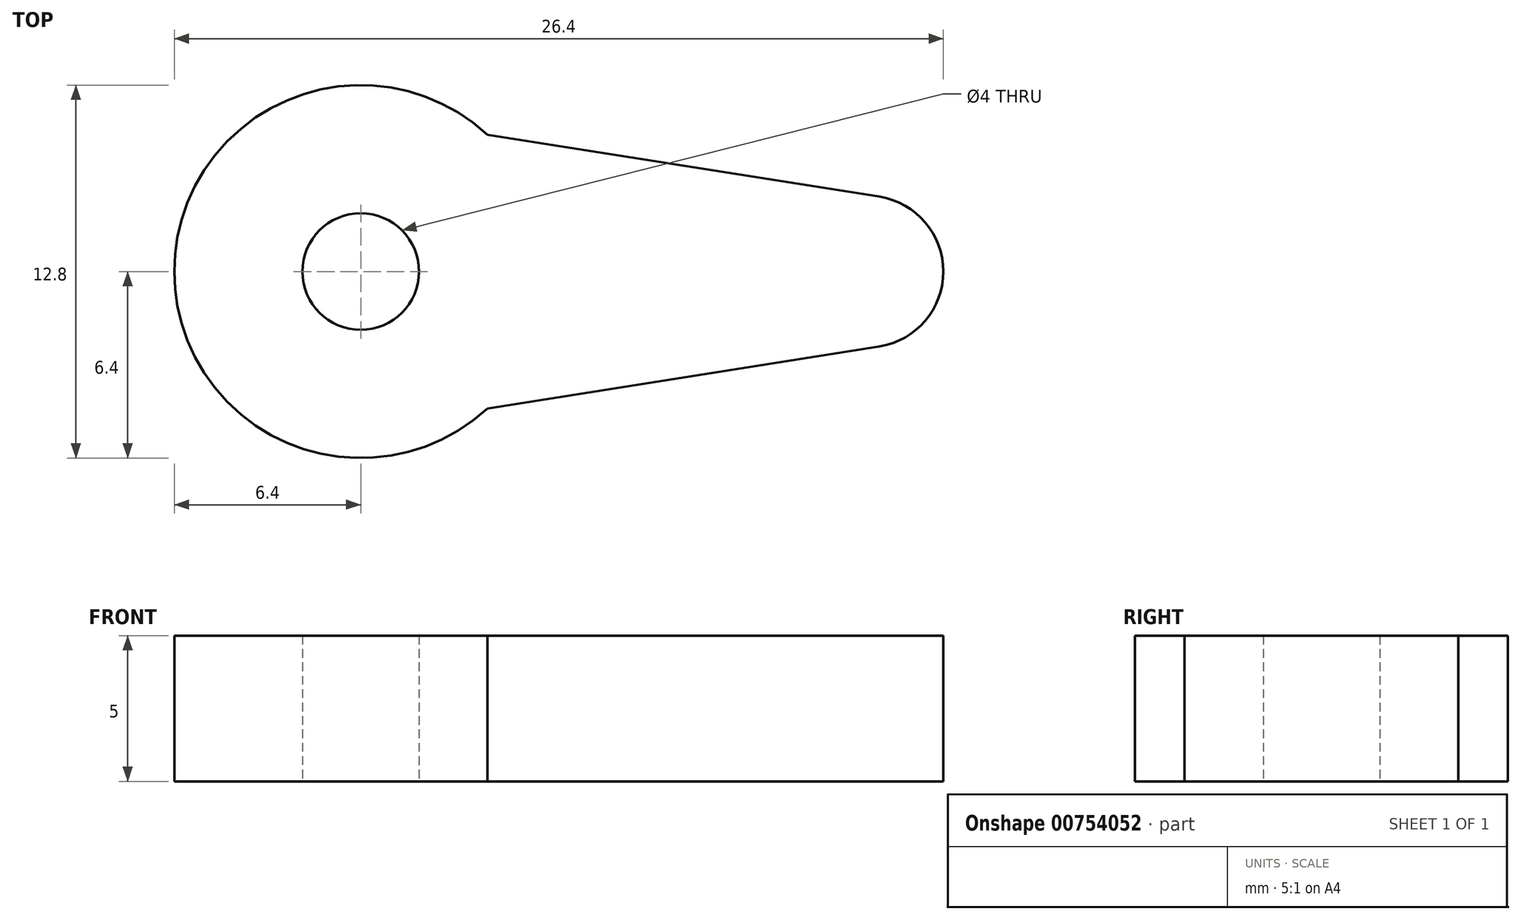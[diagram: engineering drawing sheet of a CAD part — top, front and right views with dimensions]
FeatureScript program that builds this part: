
annotation { "Feature Type Name" : "Feature", "Feature Type Description" : "" }
export const myFeature = defineFeature(function(context is Context, id is Id, definition is map)
    precondition{}
    {
        {
            var Q0;
            Q0=qCreatedBy(makeId("Top.planeOp"),FACE);
            var sketch = newSketch(context, id + "F0", { "sketchPlane" : qUnion([Q0])});
            skArc(sketch, "E0", {"start": v(4.34, 4.7) * mm, "mid": v(-6.4, 0) * mm, "end": v(4.34, -4.7) * mm});
            skLineSegment(sketch, "E1", {"start": v(0, 0) * mm, "end": v(17.4, 0) * mm, "construction": true});
            skArc(sketch, "E2", {"start": v(17.8, -2.57) * mm, "mid": v(20, 0) * mm, "end": v(17.8, 2.57) * mm});
            skLineSegment(sketch, "E3", {"start": v(4.34, 4.7) * mm, "end": v(17.8, 2.57) * mm});
            skLineSegment(sketch, "E4.MirrorCS", {"start": v(4.34, -4.7) * mm, "end": v(17.8, -2.57) * mm});
            skCircle(sketch, "E5", {"center": v(0, 0) * mm, "radius": 2 * mm});
            skSolve(sketch);
        }
        {
            var Q0;
            Q0 = qSketchRegion(id + "F0", true);
            extrude(context, id + "F1", {"entities" : qUnion([Q0]), "depth" : 5 * mm, "offsetDistance" : 25 * mm});
        }
    });
